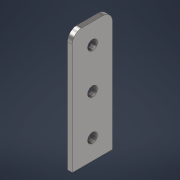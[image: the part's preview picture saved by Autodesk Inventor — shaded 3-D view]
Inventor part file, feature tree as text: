
AUTODESK INVENTOR PART (.ipt)
format: ipt  version: 2021 (Build 250183000, 183)  size: 124,928 bytes
history: native  units: mm
features: extrude x1, hole x1, fillet x1, sketch x1
ambient origin geometry x8: Origin, YZ Plane, XZ Plane, XY Plane, X Axis, Y Axis, Z Axis, Center Point
bodies: Solid1 (feature_tree)
feature tree (4):
  extrude  "Extrusion1"  Depth=50.0mm
  hole  "Hole2"  [1 undecoded]
  fillet  "Fillet3"  Radius=75.0mm
  sketch  "Sketch1"  dims[d0=150.0mm d1=50.0mm d2=25.0mm d3=75.0mm d4=6.0mm d5=0.0mm d15=50.0mm d16=50.0mm d17=12.0mm d18=6.0mm d19=4.0mm d20=2.0mm d21=90.0deg d22=8.0mm d23=20.594885mm d24=12.0mm]
note: 1 required parameter value undecoded (feature->parameter linkage not recoverable at this tier; creation-order binding heuristic only, values carry confidence <= 0.55)
